# Revit family: DWO1_63_UN_Surface-mounted_ETK
name_source: partatom
category: Lighting Fixtures
units: mm (PartAtom-declared; Revit-internal decimal feet)

## family parameters
Always vertical = Yes
Cut with Voids When Loaded = No
Light Source = No
OmniClass Number = 23.80.70.11.14.11
OmniClass Title = Downlights
Part Type = Normal
Room Calculation Point = Yes
Round Connector Dimension = Use Diameter
Shared = No
Work Plane-Based = No

## types (4) — shared parameters
Assembly Code = 63.0
Bundle = -
IfcExportAs = IfcLightFixtureType
IfcExportType = USERDEFINED
Lamp = LED
Manufacturer = ETK licht B.V.
Model = DWO.1
URL = http://www.etk.nl
Voltage = 230 V

## per-type parameters (varying)
| type | Apparent Load | Hoogte | Light Source | Radius | Wattage Comments |
| DWO.1100.15 - 16W / 1300lm / 3000K | 16 VA | 100 mm  [stored 0.328084 ft] | DWO.1 - Lightsource : DWO.1100.15 - 16W / 1300lm / 3000K | 65 mm | 16W |
| DWO.1102.15 - 16W / 1300lm / 3000K | 16 VA | 100 mm  [stored 0.328084 ft] | DWO.1 - Lightsource : DWO.1102.15 - 16W / 1300lm / 3000K | 65 mm | 16W |
| DWO.1300.15 - 25W / 2400lm / 3000K | 25 VA | 130 mm  [stored 0.426509 ft] | DWO.1 - Lightsource : DWO.1300.15 - 25W / 2400lm / 3000K | 98 mm | 25W |
| DWO.1302.15 - 25W / 2400lm / 3000K | 25 VA | 130 mm  [stored 0.426509 ft] | DWO.1 - Lightsource : DWO.1302.15 - 25W / 2400lm / 3000K | 98 mm | 25W |

note: [stored X ft] marks values corroborated as IEEE doubles in the binary element streams (Revit-internal decimal feet)

## geometry (parser evidence)
native form markers: Sweep x5
no freeform markers — native parametric forms only
